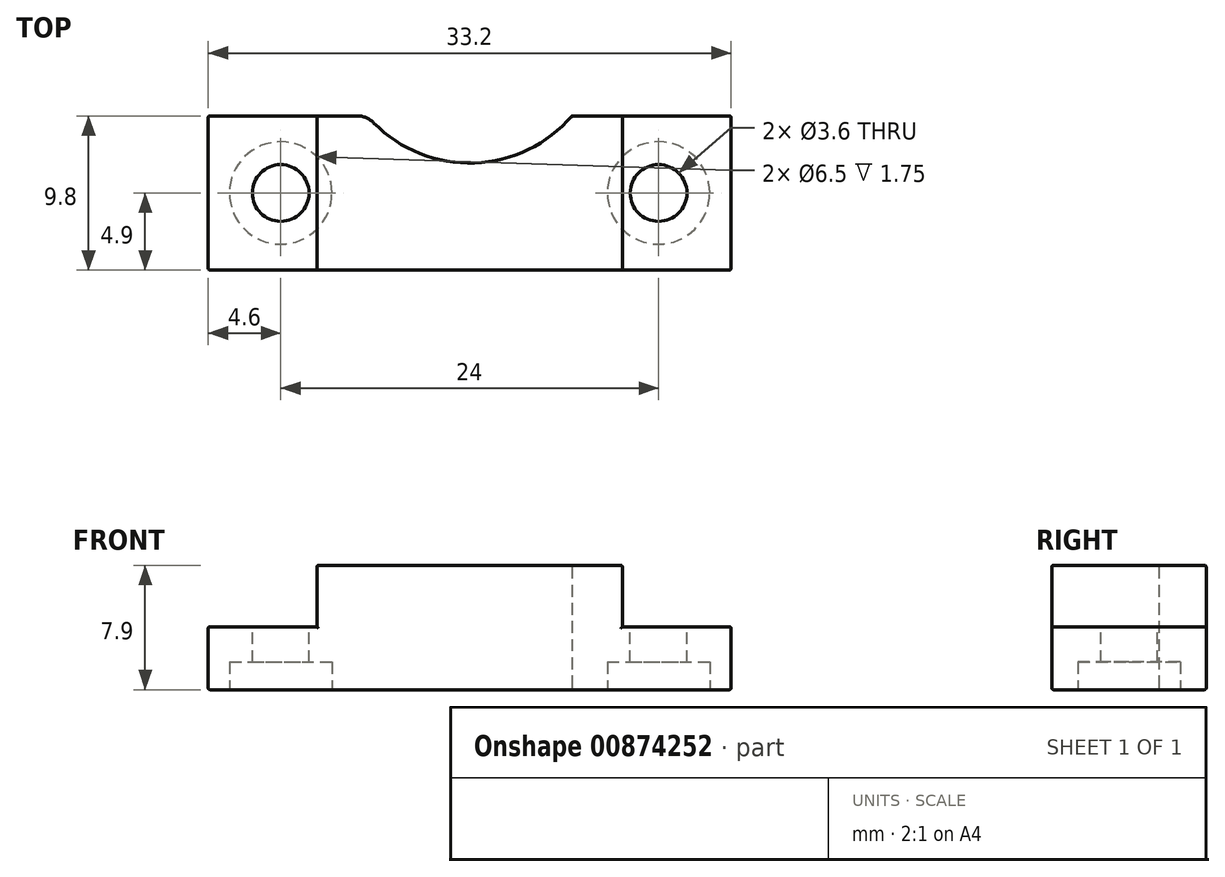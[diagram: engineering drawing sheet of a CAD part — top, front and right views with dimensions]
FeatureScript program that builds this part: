
annotation { "Feature Type Name" : "Feature", "Feature Type Description" : "" }
export const myFeature = defineFeature(function(context is Context, id is Id, definition is map)
    precondition{}
    {
        {
            var Q0;
            Q0=qCreatedBy(makeId("Top.planeOp"),FACE);
            var sketch = newSketch(context, id + "F0", { "sketchPlane" : qUnion([Q0])});
            skCircle(sketch, "E0", {"center": v(-12, 0) * mm, "radius": 1.8 * mm});
            skCircle(sketch, "E1", {"center": v(12, 0) * mm, "radius": 1.8 * mm});
            skLineSegment(sketch, "E2.bottom", {"start": v(16.6, -4.9) * mm, "end": v(-16.6, -4.9) * mm});
            skLineSegment(sketch, "E2.top", {"start": v(16.6, 4.9) * mm, "end": v(-16.6, 4.9) * mm});
            skLineSegment(sketch, "E2.left", {"start": v(16.6, -4.9) * mm, "end": v(16.6, 4.9) * mm});
            skLineSegment(sketch, "E2.right", {"start": v(-16.6, -4.9) * mm, "end": v(-16.6, 4.9) * mm});
            skPoint(sketch, "E2.middle", {"position": v(0, 0) * mm});
            skSolve(sketch);
        }
        {
            var Q0;
            Q0=makeQuery(id+"F0.imprint","IMPRINT",FACE,{"disambiguationData":[TD([[makeQuery(id+"F0.imprint","IMPRINT",EDGE,{"derivedFrom":sQuery(id+"F0.wireOp",EDGE,"E0")}),-1.0]])]});
            extrude(context, id + "F1", {"entities" : qUnion([Q0]), "oppositeDirection" : true, "depth" : 4 * mm, "offsetDistance" : 25 * mm});
        }
        {
            var Q0;
            Q0=makeQuery(id+"F1.opExtrude","CAP_FACE",FACE,{"disambiguationData":[OSD([sQuery(id+"F0.wireOp",EDGE,"E0"),sQuery(id+"F0.wireOp",EDGE,"E1"),sQuery(id+"F0.wireOp",EDGE,"E2.bottom"),sQuery(id+"F0.wireOp",EDGE,"E2.top"),sQuery(id+"F0.wireOp",EDGE,"E2.left"),sQuery(id+"F0.wireOp",EDGE,"E2.right")])],"isStart":true});
            var sketch = newSketch(context, id + "F2", { "sketchPlane" : qUnion([Q0])});
            skLineSegment(sketch, "E3.bottom", {"start": v(9.7, 4.9) * mm, "end": v(-9.7, 4.9) * mm});
            skLineSegment(sketch, "E3.top", {"start": v(9.7, -4.9) * mm, "end": v(-9.7, -4.9) * mm});
            skLineSegment(sketch, "E3.left", {"start": v(9.7, 4.9) * mm, "end": v(9.7, -4.9) * mm});
            skLineSegment(sketch, "E3.right", {"start": v(-9.7, 4.9) * mm, "end": v(-9.7, -4.9) * mm});
            skPoint(sketch, "E3.middle", {"position": v(0, 0) * mm});
            skSolve(sketch);
        }
        {
            var Q0;
            Q0 = qSketchRegion(id + "F2", true);
            extrude(context, id + "F3", {"entities" : qUnion([Q0]), "operationType" : NewBodyOperationType.ADD, "depth" : 3.9 * mm, "offsetDistance" : 25 * mm});
        }
        {
            var Q0;
            Q0=makeQuery(id+"F1.opExtrude","CAP_FACE",FACE,{"disambiguationData":[OSD([sQuery(id+"F0.wireOp",EDGE,"E0"),sQuery(id+"F0.wireOp",EDGE,"E1"),sQuery(id+"F0.wireOp",EDGE,"E2.bottom"),sQuery(id+"F0.wireOp",EDGE,"E2.top"),sQuery(id+"F0.wireOp",EDGE,"E2.left"),sQuery(id+"F0.wireOp",EDGE,"E2.right")])],"isStart":false});
            var sketch = newSketch(context, id + "F4", { "sketchPlane" : qUnion([Q0])});
            skCircle(sketch, "E4", {"center": v(-12, 0) * mm, "radius": 3.25 * mm});
            skCircle(sketch, "E5", {"center": v(12, 0) * mm, "radius": 3.25 * mm});
            skSolve(sketch);
        }
        {
            var Q0;
            Q0 = qSketchRegion(id + "F4", true);
            extrude(context, id + "F5", {"entities" : qUnion([Q0]), "operationType" : NewBodyOperationType.REMOVE, "oppositeDirection" : true, "depth" : 1.75 * mm, "offsetDistance" : 25 * mm});
        }
        {
            var Q0;
            {var subQ0=sQuery(id+"F0.wireOp",EDGE,"E2.left");var subQ1=sQuery(id+"F0.wireOp",EDGE,"E2.top");var subQ2=sQuery(id+"F0.wireOp",EDGE,"E2.bottom");var subQ3=sQuery(id+"F0.wireOp",EDGE,"E1");Q0=makeQuery(id+"F3.boolean.opBoolean","SPLIT",FACE,{"disambiguationData":[TD([makeQuery(id+"F1.opExtrude","SWEPT_FACE",FACE,{"disambiguationData":[OSD([subQ3])]})])],"derivedFrom":makeQuery(id+"F1.opExtrude","CAP_FACE",FACE,{"disambiguationData":[OSD([sQuery(id+"F0.wireOp",EDGE,"E0"),subQ3,subQ2,subQ1,subQ0,sQuery(id+"F0.wireOp",EDGE,"E2.right")])],"isStart":true})});}
            var sketch = newSketch(context, id + "F6", { "sketchPlane" : qUnion([Q0])});
            skArc(sketch, "E6", {"start": v(6.5, 4.9) * mm, "mid": v(0, 1.9) * mm, "end": v(-6.5, 4.9) * mm});
            skLineSegment(sketch, "E7", {"start": v(6.5, 4.9) * mm, "end": v(-6.5, 4.9) * mm});
            skSolve(sketch);
        }
        {
            var Q0;
            Q0 = qSketchRegion(id + "F6", true);
            extrude(context, id + "F7", {"entities" : qUnion([Q0]), "operationType" : NewBodyOperationType.REMOVE, "endBound" : BoundingType.THROUGH_ALL, "depth" : 25 * mm, "offsetDistance" : 25 * mm, "hasSecondDirection" : true, "secondDirectionBound" : SecondDirectionBoundingType.THROUGH_ALL, "secondDirectionOppositeDirection" : true, "secondDirectionDepth" : 25 * mm});
        }
        {
            var Q0;
            Q0=makeQuery(id+"F3.opExtrude","SWEPT_EDGE",EDGE,{"disambiguationData":[OSD([sQuery(id+"F0.wireOp",EDGE,"E2.top"),sQuery(id+"F2.wireOp",EDGE,"E3.bottom"),sQuery(id+"F2.wireOp",EDGE,"E3.right")])]});
            var Q1;
            {var subQ0=sQuery(id+"F0.wireOp",EDGE,"E2.right");var subQ1=sQuery(id+"F0.wireOp",EDGE,"E2.top");Q1=makeQuery(id+"F3.boolean.opBoolean","SPLIT",EDGE,{"disambiguationData":[TD([makeQuery(id+"F1.opExtrude","SWEPT_FACE",FACE,{"disambiguationData":[OSD([subQ0])]})])],"derivedFrom":makeQuery(id+"F1.opExtrude","CAP_EDGE",EDGE,{"disambiguationData":[OSD([subQ1])],"isStart":true})});}
            var Q2;
            Q2=makeQuery(id+"F3.opExtrude","CAP_EDGE",EDGE,{"disambiguationData":[OSD([sQuery(id+"F2.wireOp",EDGE,"E3.bottom")])],"isStart":false});
            var Q3;
            Q3=makeQuery(id+"F3.opExtrude","SWEPT_EDGE",EDGE,{"disambiguationData":[OSD([sQuery(id+"F0.wireOp",EDGE,"E2.top"),sQuery(id+"F2.wireOp",EDGE,"E3.bottom"),sQuery(id+"F2.wireOp",EDGE,"E3.left")])]});
            var Q4;
            {var subQ0=sQuery(id+"F0.wireOp",EDGE,"E2.left");var subQ1=sQuery(id+"F0.wireOp",EDGE,"E2.top");Q4=makeQuery(id+"F3.boolean.opBoolean","SPLIT",EDGE,{"disambiguationData":[TD([makeQuery(id+"F1.opExtrude","SWEPT_FACE",FACE,{"disambiguationData":[OSD([subQ0])]})])],"derivedFrom":makeQuery(id+"F1.opExtrude","CAP_EDGE",EDGE,{"disambiguationData":[OSD([subQ1])],"isStart":true})});}
            var Q5;
            Q5=makeQuery(id+"F1.opExtrude","CAP_EDGE",EDGE,{"disambiguationData":[OSD([sQuery(id+"F0.wireOp",EDGE,"E2.top")])],"isStart":false});
            var Q6;
            Q6=makeQuery(id+"F1.opExtrude","SWEPT_EDGE",EDGE,{"disambiguationData":[OSD([sQuery(id+"F0.wireOp",EDGE,"E2.top"),sQuery(id+"F0.wireOp",EDGE,"E2.left")])]});
            var Q7;
            Q7=makeQuery(id+"F1.opExtrude","SWEPT_EDGE",EDGE,{"disambiguationData":[OSD([sQuery(id+"F0.wireOp",EDGE,"E2.top"),sQuery(id+"F0.wireOp",EDGE,"E2.right")])]});
            var Q8;
            Q8=makeQuery(id+"F1.opExtrude","CAP_EDGE",EDGE,{"disambiguationData":[OSD([sQuery(id+"F0.wireOp",EDGE,"E2.right")])],"isStart":false});
            var Q9;
            Q9=makeQuery(id+"F1.opExtrude","CAP_EDGE",EDGE,{"disambiguationData":[OSD([sQuery(id+"F0.wireOp",EDGE,"E2.right")])],"isStart":true});
            var Q10;
            Q10=makeQuery(id+"F3.opExtrude","CAP_EDGE",EDGE,{"disambiguationData":[OSD([sQuery(id+"F2.wireOp",EDGE,"E3.right")])],"isStart":false});
            var Q11;
            Q11=makeQuery(id+"F3.opExtrude","CAP_EDGE",EDGE,{"disambiguationData":[OSD([sQuery(id+"F2.wireOp",EDGE,"E3.left")])],"isStart":false});
            var Q12;
            Q12=makeQuery(id+"F1.opExtrude","CAP_EDGE",EDGE,{"disambiguationData":[OSD([sQuery(id+"F0.wireOp",EDGE,"E2.left")])],"isStart":true});
            var Q13;
            Q13=makeQuery(id+"F1.opExtrude","CAP_EDGE",EDGE,{"disambiguationData":[OSD([sQuery(id+"F0.wireOp",EDGE,"E2.left")])],"isStart":false});
            var Q14;
            Q14=makeQuery(id+"F1.opExtrude","CAP_EDGE",EDGE,{"disambiguationData":[OSD([sQuery(id+"F0.wireOp",EDGE,"E2.bottom")])],"isStart":false});
            var Q15;
            Q15=makeQuery(id+"F1.opExtrude","SWEPT_EDGE",EDGE,{"disambiguationData":[OSD([sQuery(id+"F0.wireOp",EDGE,"E2.bottom"),sQuery(id+"F0.wireOp",EDGE,"E2.left")])]});
            var Q16;
            Q16=makeQuery(id+"F3.opExtrude","CAP_EDGE",EDGE,{"disambiguationData":[OSD([sQuery(id+"F2.wireOp",EDGE,"E3.top")])],"isStart":false});
            var Q17;
            Q17=makeQuery(id+"F3.opExtrude","SWEPT_EDGE",EDGE,{"disambiguationData":[OSD([sQuery(id+"F0.wireOp",EDGE,"E2.bottom"),sQuery(id+"F2.wireOp",EDGE,"E3.top"),sQuery(id+"F2.wireOp",EDGE,"E3.left")])]});
            var Q18;
            {var subQ0=sQuery(id+"F0.wireOp",EDGE,"E2.bottom");var subQ1=sQuery(id+"F0.wireOp",EDGE,"E2.left");Q18=makeQuery(id+"F3.boolean.opBoolean","SPLIT",EDGE,{"disambiguationData":[TD([makeQuery(id+"F1.opExtrude","SWEPT_FACE",FACE,{"disambiguationData":[OSD([subQ1])]})])],"derivedFrom":makeQuery(id+"F1.opExtrude","CAP_EDGE",EDGE,{"disambiguationData":[OSD([subQ0])],"isStart":true})});}
            var Q19;
            {var subQ0=sQuery(id+"F0.wireOp",EDGE,"E2.right");var subQ1=sQuery(id+"F0.wireOp",EDGE,"E2.bottom");Q19=makeQuery(id+"F3.boolean.opBoolean","SPLIT",EDGE,{"disambiguationData":[TD([makeQuery(id+"F1.opExtrude","SWEPT_FACE",FACE,{"disambiguationData":[OSD([subQ0])]})])],"derivedFrom":makeQuery(id+"F1.opExtrude","CAP_EDGE",EDGE,{"disambiguationData":[OSD([subQ1])],"isStart":true})});}
            var Q20;
            Q20=makeQuery(id+"F3.opExtrude","SWEPT_EDGE",EDGE,{"disambiguationData":[OSD([sQuery(id+"F0.wireOp",EDGE,"E2.bottom"),sQuery(id+"F2.wireOp",EDGE,"E3.top"),sQuery(id+"F2.wireOp",EDGE,"E3.right")])]});
            var Q21;
            Q21=makeQuery(id+"F1.opExtrude","SWEPT_EDGE",EDGE,{"disambiguationData":[OSD([sQuery(id+"F0.wireOp",EDGE,"E2.bottom"),sQuery(id+"F0.wireOp",EDGE,"E2.right")])]});
            var Q22;
            Q22=makeQuery(id+"F7.boolean.opBoolean","INTERSECT",EDGE,{"derivedFrom":[makeQuery(id+"F3.opExtrude","CAP_FACE",FACE,{"disambiguationData":[OSD([sQuery(id+"F2.wireOp",EDGE,"E3.bottom"),sQuery(id+"F2.wireOp",EDGE,"E3.top"),sQuery(id+"F2.wireOp",EDGE,"E3.left"),sQuery(id+"F2.wireOp",EDGE,"E3.right")])],"isStart":false}),makeQuery(id+"F7.opExtrude","SWEPT_FACE",FACE,{"disambiguationData":[OSD([sQuery(id+"F6.wireOp",EDGE,"E6")])]})]});
            var Q23;
            Q23=makeQuery(id+"F7.boolean.opBoolean","INTERSECT",EDGE,{"derivedFrom":[makeQuery(id+"F1.opExtrude","CAP_FACE",FACE,{"disambiguationData":[OSD([sQuery(id+"F0.wireOp",EDGE,"E0"),sQuery(id+"F0.wireOp",EDGE,"E1"),sQuery(id+"F0.wireOp",EDGE,"E2.bottom"),sQuery(id+"F0.wireOp",EDGE,"E2.top"),sQuery(id+"F0.wireOp",EDGE,"E2.left"),sQuery(id+"F0.wireOp",EDGE,"E2.right")])],"isStart":false}),makeQuery(id+"F7.opExtrude","SWEPT_FACE",FACE,{"disambiguationData":[OSD([sQuery(id+"F6.wireOp",EDGE,"E6")])]})]});
            fillet(context, id + "F8", {"entities" : qUnion([Q0, Q1, Q2, Q3, Q4, Q5, Q6, Q7, Q8, Q9, Q10, Q11, Q12, Q13, Q14, Q15, Q16, Q17, Q18, Q19, Q20, Q21, Q22, Q23]), "radius" : .1 * mm, "tangentPropagation" : true, "allowEdgeOverflow" : false});
        }
        {
            var Q0;
            {var subQ0=sQuery(id+"F6.wireOp",EDGE,"E7");var subQ1=sQuery(id+"F6.wireOp",EDGE,"E6");Q0=makeQuery(id+"F7.boolean.opBoolean","COPY",EDGE,{"derivedFrom":makeQuery(id+"F7.opExtrude","SWEPT_EDGE",EDGE,{"disambiguationData":[OSD([subQ1,subQ0]),TDD([makeQuery(id+"F6.imprint","INTERSECT",VERTEX,{"disambiguationData":[OD(1.0)],"derivedFrom":[subQ1,subQ0]})])]})});}
            var Q1;
            {var subQ0=sQuery(id+"F6.wireOp",EDGE,"E7");var subQ1=sQuery(id+"F6.wireOp",EDGE,"E6");Q1=makeQuery(id+"F7.boolean.opBoolean","COPY",EDGE,{"derivedFrom":makeQuery(id+"F7.opExtrude","SWEPT_EDGE",EDGE,{"disambiguationData":[OSD([subQ1,subQ0]),TDD([makeQuery(id+"F6.imprint","INTERSECT",VERTEX,{"disambiguationData":[OD(0.0)],"derivedFrom":[subQ1,subQ0]})])]})});}
            fillet(context, id + "F9", {"entities" : qUnion([Q0, Q1]), "radius" : 1.5 * mm, "tangentPropagation" : true, "allowEdgeOverflow" : false});
        }
    });
